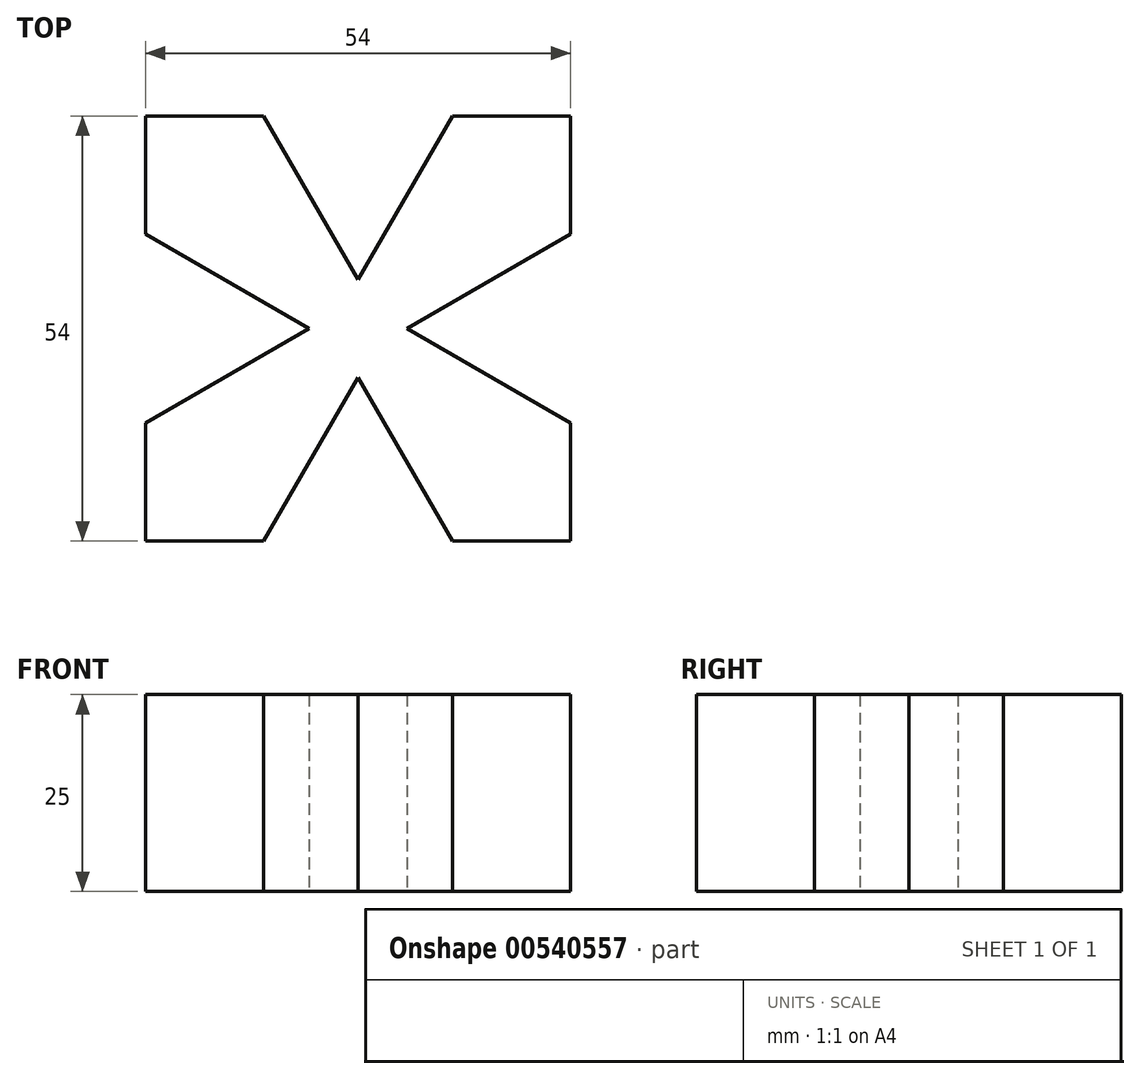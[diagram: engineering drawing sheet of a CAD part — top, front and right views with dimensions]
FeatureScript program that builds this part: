
annotation { "Feature Type Name" : "Feature", "Feature Type Description" : "" }
export const myFeature = defineFeature(function(context is Context, id is Id, definition is map)
    precondition{}
    {
        {
            var Q0;
            Q0=qCreatedBy(makeId("Top.planeOp"),FACE);
            var sketch = newSketch(context, id + "F0", { "sketchPlane" : qUnion([Q0])});
            skLineSegment(sketch, "E0", {"start": v(-11.77, -44.12) * mm, "end": v(3.23, -44.12) * mm});
            skLineSegment(sketch, "E1", {"start": v(3.23, -44.12) * mm, "end": v(15.23, -23.34) * mm});
            skLineSegment(sketch, "E2", {"start": v(15.23, -23.34) * mm, "end": v(27.23, -44.12) * mm});
            skLineSegment(sketch, "E3.trimOffspring", {"start": v(27.23, -44.12) * mm, "end": v(42.23, -44.12) * mm});
            skLineSegment(sketch, "E4", {"start": v(42.23, -44.12) * mm, "end": v(42.23, -29.12) * mm});
            skLineSegment(sketch, "E5", {"start": v(42.23, -29.12) * mm, "end": v(21.44, -17.12) * mm});
            skLineSegment(sketch, "E6", {"start": v(21.44, -17.12) * mm, "end": v(42.23, -5.12) * mm});
            skLineSegment(sketch, "E7.trimOffspring", {"start": v(42.23, -5.12) * mm, "end": v(42.23, 9.88) * mm});
            skLineSegment(sketch, "E8", {"start": v(42.23, 9.88) * mm, "end": v(27.23, 9.88) * mm});
            skLineSegment(sketch, "E9", {"start": v(3.23, 9.88) * mm, "end": v(15.23, -10.9) * mm});
            skLineSegment(sketch, "E10", {"start": v(15.23, -10.9) * mm, "end": v(27.23, 9.88) * mm});
            skLineSegment(sketch, "E11.trimOffspring", {"start": v(3.23, 9.88) * mm, "end": v(-11.77, 9.88) * mm});
            skLineSegment(sketch, "E12", {"start": v(-11.77, 9.88) * mm, "end": v(-11.77, -5.12) * mm});
            skPoint(sketch, "E13.trimOffspring.start.orphan", {"position": v(-11.77, -17.12) * mm});
            skLineSegment(sketch, "E14", {"start": v(-11.77, -44.12) * mm, "end": v(-11.77, -29.12) * mm});
            skLineSegment(sketch, "E15", {"start": v(-11.77, -5.12) * mm, "end": v(9, -17.12) * mm});
            skLineSegment(sketch, "E16", {"start": v(9, -17.12) * mm, "end": v(-11.77, -29.12) * mm});
            skSolve(sketch);
        }
        {
            var Q0;
            Q0=makeQuery(id+"F0.imprint","IMPRINT",FACE,{"disambiguationData":[TD([[makeQuery(id+"F0.imprint","IMPRINT",EDGE,{"derivedFrom":sQuery(id+"F0.wireOp",EDGE,"E0")}),1.0]])]});
            extrude(context, id + "F1", {"entities" : qUnion([Q0]), "depth" : 25 * mm, "offsetDistance" : 25 * mm});
        }
    });
